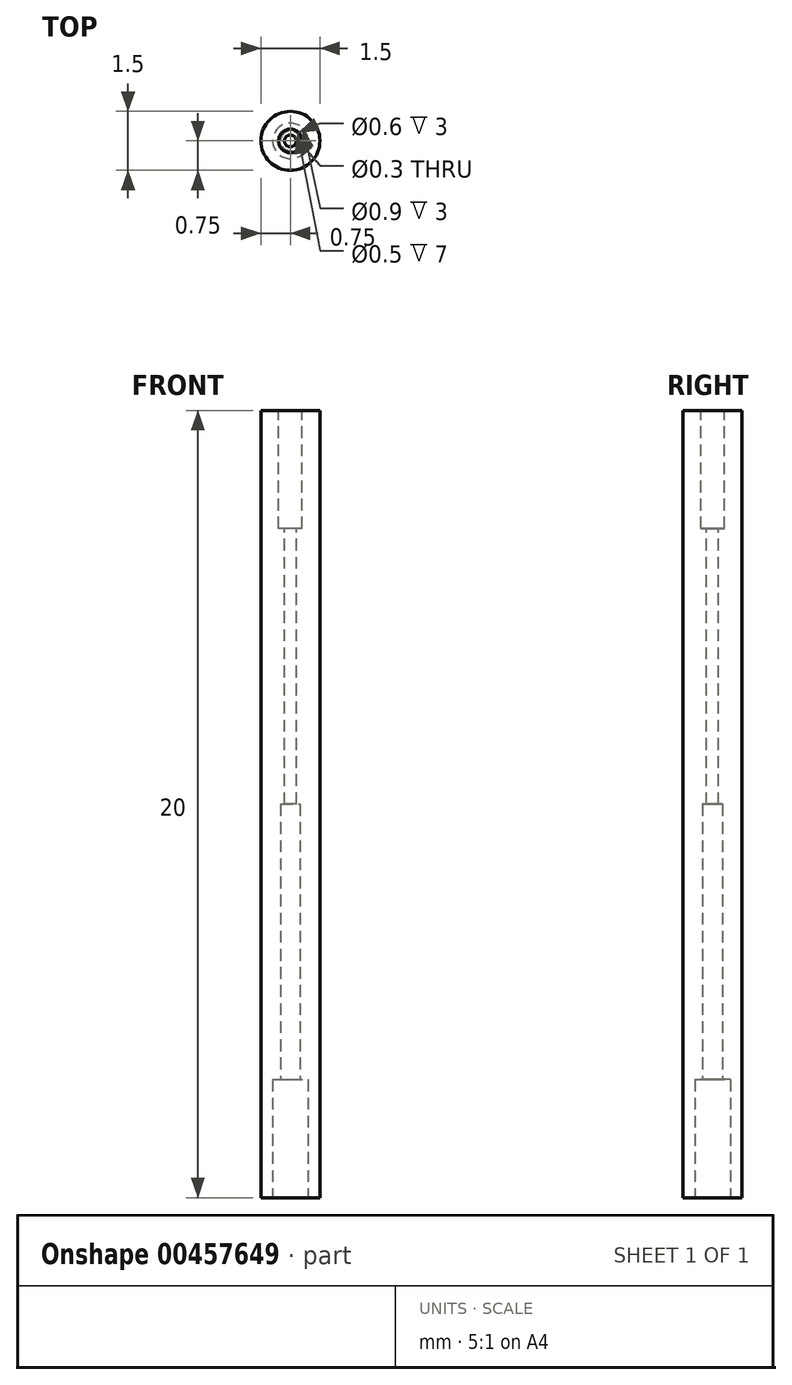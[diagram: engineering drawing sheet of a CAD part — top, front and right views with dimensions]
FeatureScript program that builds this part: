
annotation { "Feature Type Name" : "Feature", "Feature Type Description" : "" }
export const myFeature = defineFeature(function(context is Context, id is Id, definition is map)
    precondition{}
    {
        {
            var Q0;
            Q0=qCreatedBy(makeId("Top.planeOp"),FACE);
            var sketch = newSketch(context, id + "F0", { "sketchPlane" : qUnion([Q0])});
            skCircle(sketch, "E0", {"center": v(0, 0) * mm, "radius": 0.75 * mm});
            skSolve(sketch);
        }
        {
            var Q0;
            Q0 = qSketchRegion(id + "F0", true);
            extrude(context, id + "F1", {"entities" : qUnion([Q0]), "depth" : 20 * mm, "offsetDistance" : 25 * mm});
        }
        {
            var Q0;
            Q0=makeQuery(id+"F1.opExtrude","CAP_FACE",FACE,{"disambiguationData":[OSD([sQuery(id+"F0.wireOp",EDGE,"E0")])],"isStart":false});
            var sketch = newSketch(context, id + "F2", { "sketchPlane" : qUnion([Q0])});
            skCircle(sketch, "E1", {"center": v(0, 0) * mm, "radius": 0.3 * mm});
            skSolve(sketch);
        }
        {
            var Q0;
            Q0 = qSketchRegion(id + "F2", true);
            extrude(context, id + "F3", {"entities" : qUnion([Q0]), "operationType" : NewBodyOperationType.REMOVE, "oppositeDirection" : true, "depth" : 3 * mm});
        }
        {
            var Q0;
            Q0=makeQuery(id+"F3.boolean.opBoolean","COPY",FACE,{"derivedFrom":makeQuery(id+"F3.opExtrude","CAP_FACE",FACE,{"disambiguationData":[OSD([sQuery(id+"F2.wireOp",EDGE,"E1")])],"isStart":false})});
            var sketch = newSketch(context, id + "F4", { "sketchPlane" : qUnion([Q0])});
            skCircle(sketch, "E2", {"center": v(0, 0) * mm, "radius": 0.15 * mm});
            skSolve(sketch);
        }
        {
            var Q0;
            Q0=makeQuery(id+"F4.imprint","IMPRINT",FACE,{"disambiguationData":[TD([[makeQuery(id+"F4.imprint","IMPRINT",EDGE,{"derivedFrom":sQuery(id+"F4.wireOp",EDGE,"E2")}),1.0]])]});
            extrude(context, id + "F5", {"entities" : qUnion([Q0]), "operationType" : NewBodyOperationType.REMOVE, "oppositeDirection" : true, "depth" : 7 * mm});
        }
        {
            var Q0;
            Q0=makeQuery(id+"F1.opExtrude","CAP_FACE",FACE,{"disambiguationData":[OSD([sQuery(id+"F0.wireOp",EDGE,"E0")])],"isStart":true});
            var sketch = newSketch(context, id + "F6", { "sketchPlane" : qUnion([Q0])});
            skCircle(sketch, "E3", {"center": v(0, 0) * mm, "radius": 0.45 * mm});
            skSolve(sketch);
        }
        {
            var Q0;
            Q0 = qSketchRegion(id + "F6", true);
            extrude(context, id + "F7", {"entities" : qUnion([Q0]), "operationType" : NewBodyOperationType.REMOVE, "oppositeDirection" : true, "depth" : 3 * mm});
        }
        {
            var Q0;
            Q0=makeQuery(id+"F7.boolean.opBoolean","COPY",FACE,{"derivedFrom":makeQuery(id+"F7.opExtrude","CAP_FACE",FACE,{"disambiguationData":[OSD([sQuery(id+"F6.wireOp",EDGE,"E3")])],"isStart":false})});
            var sketch = newSketch(context, id + "F8", { "sketchPlane" : qUnion([Q0])});
            skCircle(sketch, "E4", {"center": v(0, 0) * mm, "radius": 0.25 * mm});
            skSolve(sketch);
        }
        {
            var Q0;
            Q0 = qSketchRegion(id + "F8", true);
            extrude(context, id + "F9", {"entities" : qUnion([Q0]), "operationType" : NewBodyOperationType.REMOVE, "oppositeDirection" : true, "depth" : 7 * mm});
        }
    });
